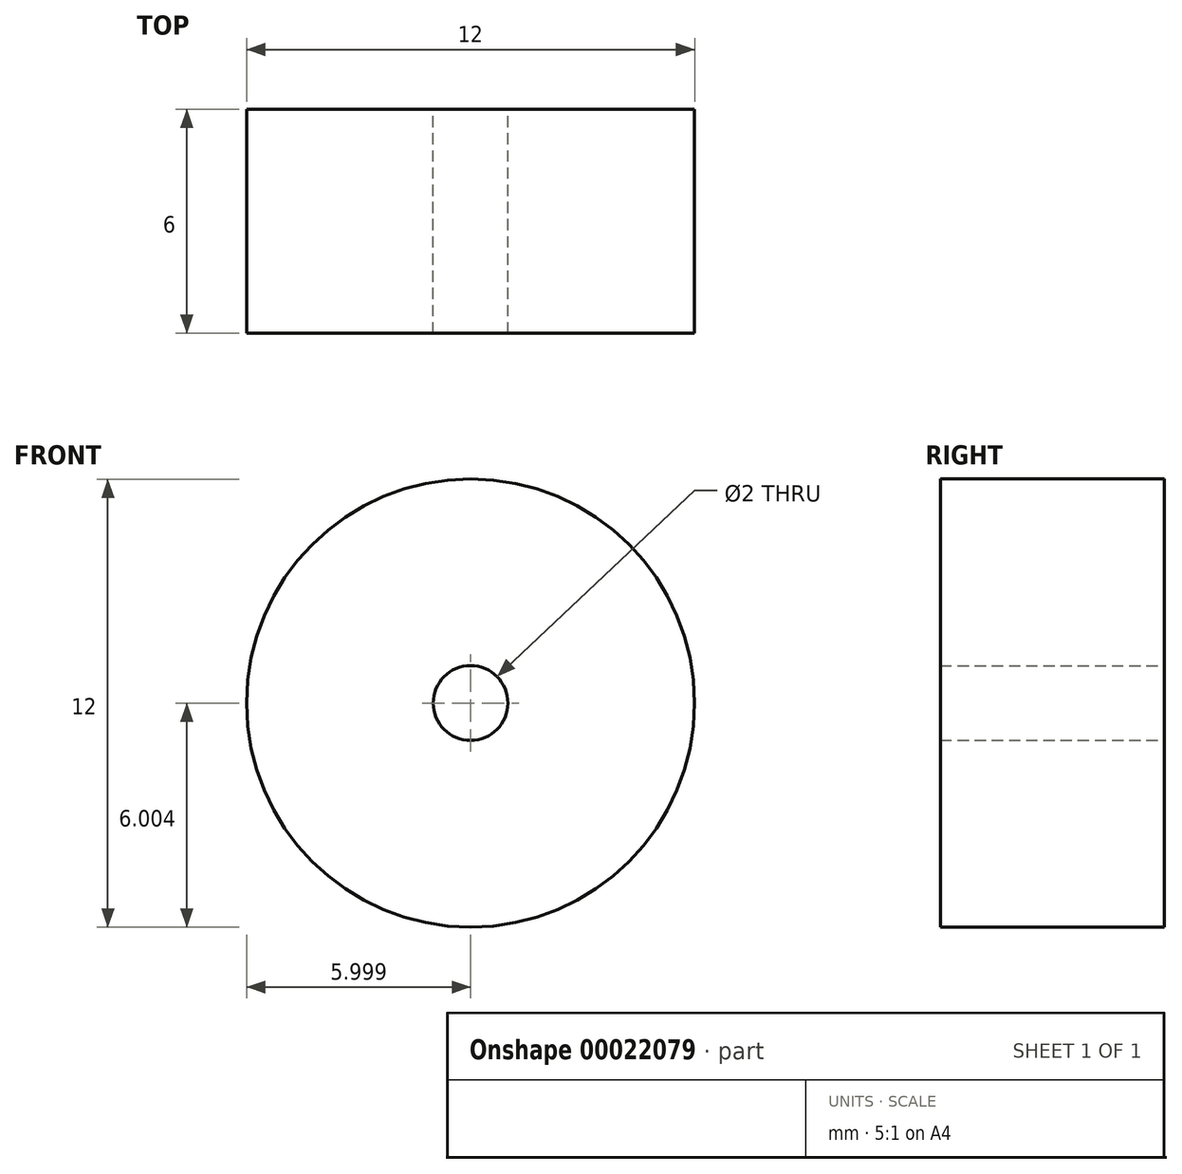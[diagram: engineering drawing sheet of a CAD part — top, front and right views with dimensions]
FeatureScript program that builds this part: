
annotation { "Feature Type Name" : "Feature", "Feature Type Description" : "" }
export const myFeature = defineFeature(function(context is Context, id is Id, definition is map)
    precondition{}
    {
        {
            var Q0;
            Q0=qCreatedBy(makeId("Front.planeOp"),FACE);
            var sketch = newSketch(context, id + "F0", { "sketchPlane" : qUnion([Q0])});
            skCircle(sketch, "E0", {"center": v(-15.45, -7.59) * mm, "radius": 6 * mm});
            skCircle(sketch, "E1", {"center": v(-15.45, -7.59) * mm, "radius": 1 * mm});
            skSolve(sketch);
        }
        {
            var Q0;
            Q0=makeQuery(id+"F0.imprint","IMPRINT",FACE,{"disambiguationData":[TD([[makeQuery(id+"F0.imprint","IMPRINT",EDGE,{"derivedFrom":sQuery(id+"F0.wireOp",EDGE,"E0")}),1.0]])]});
            extrude(context, id + "F1", {"entities" : qUnion([Q0]), "endBound" : BoundingType.SYMMETRIC, "depth" : 6 * mm});
        }
    });
